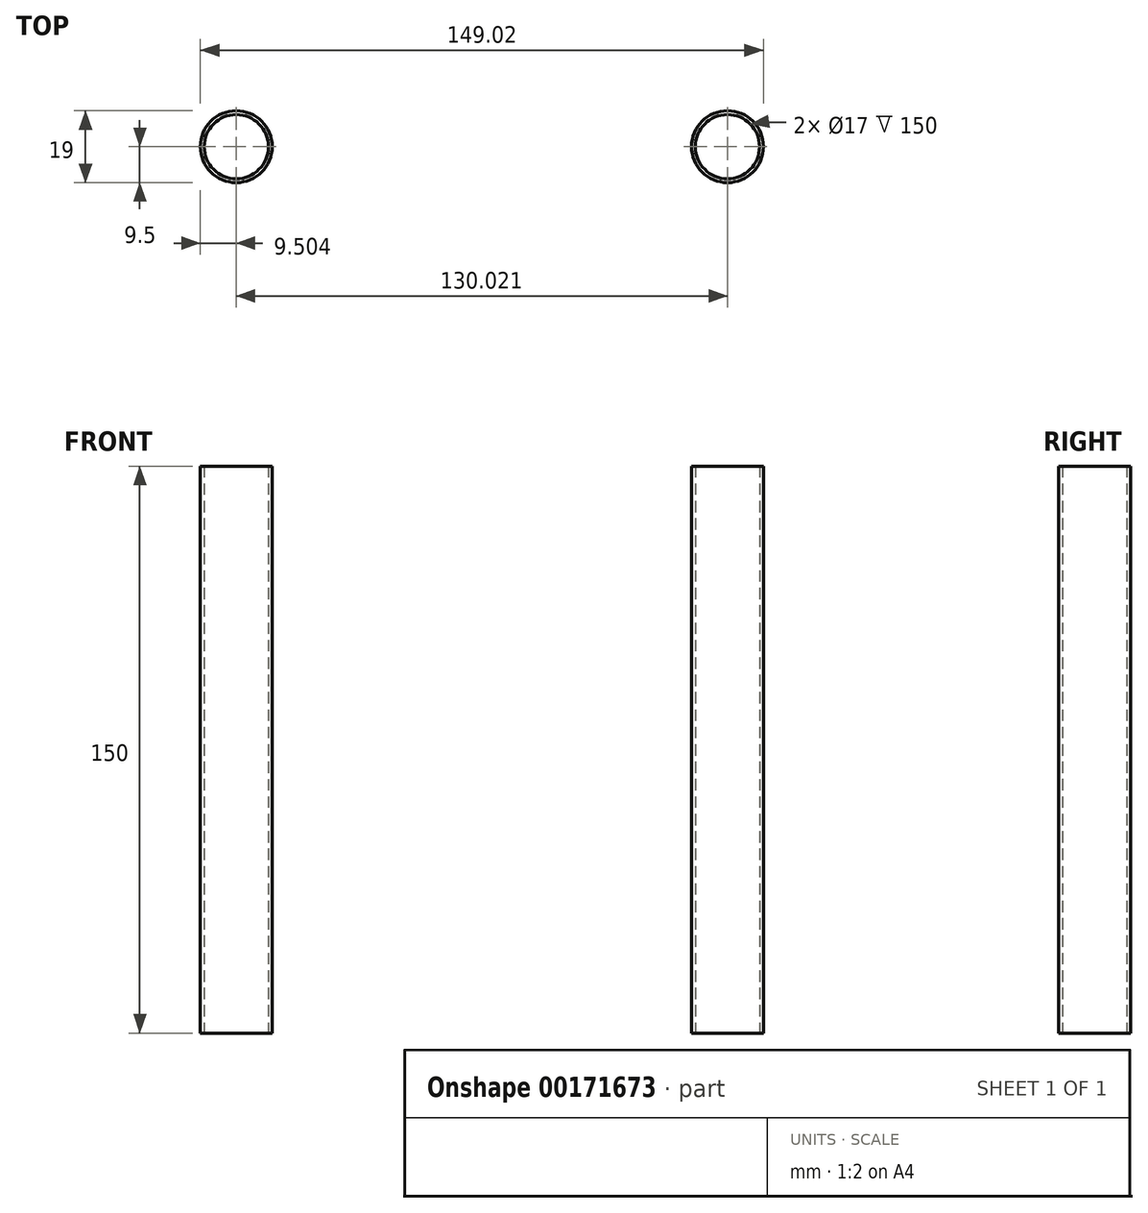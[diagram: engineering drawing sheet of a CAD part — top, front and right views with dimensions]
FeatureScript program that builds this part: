
annotation { "Feature Type Name" : "Feature", "Feature Type Description" : "" }
export const myFeature = defineFeature(function(context is Context, id is Id, definition is map)
    precondition{}
    {
        {
            var Q0;
            Q0=qCreatedBy(makeId("Top.planeOp"),FACE);
            var sketch = newSketch(context, id + "F0", { "sketchPlane" : qUnion([Q0])});
            skCircle(sketch, "E0", {"center": v(0, 0) * mm, "radius": 75 * mm});
            skCircle(sketch, "E1", {"center": v(0, 0) * mm, "radius": 55 * mm});
            skCircle(sketch, "E2", {"center": v(-64.99, 0) * mm, "radius": 9.5 * mm});
            skCircle(sketch, "E3", {"center": v(65.03, 0) * mm, "radius": 9.5 * mm});
            skSolve(sketch);
        }
        {
            var Q0;
            Q0=makeQuery(id+"F0.imprint","IMPRINT",FACE,{"disambiguationData":[TD([[makeQuery(id+"F0.imprint","IMPRINT",EDGE,{"derivedFrom":sQuery(id+"F0.wireOp",EDGE,"E0")}),1.0]])]});
            extrude(context, id + "F1", {"entities" : qUnion([Q0]), "depth" : 150 * mm});
        }
        {
            var Q0;
            Q0=makeQuery(id+"F1.opExtrude","CAP_FACE",FACE,{"disambiguationData":[OSD([sQuery(id+"F0.wireOp",EDGE,"E0"),sQuery(id+"F0.wireOp",EDGE,"E1"),sQuery(id+"F0.wireOp",EDGE,"E2"),sQuery(id+"F0.wireOp",EDGE,"E3")])],"isStart":true});
            var sketch = newSketch(context, id + "F2", { "sketchPlane" : qUnion([Q0])});
            skCircle(sketch, "E4.0", {"center": v(0, 0) * mm, "radius": 75 * mm});
            skSolve(sketch);
        }
        {
            var Q0;
            Q0 = qSketchRegion(id + "F2", true);
            extrude(context, id + "F3", {"entities" : qUnion([Q0]), "operationType" : NewBodyOperationType.ADD, "depth" : 5 * mm});
        }
        {
            var Q0;
            Q0=makeQuery(id+"F1.opExtrude","CAP_FACE",FACE,{"disambiguationData":[OSD([sQuery(id+"F0.wireOp",EDGE,"E0"),sQuery(id+"F0.wireOp",EDGE,"E1"),sQuery(id+"F0.wireOp",EDGE,"E2"),sQuery(id+"F0.wireOp",EDGE,"E3")])],"isStart":false});
            var sketch = newSketch(context, id + "F4", { "sketchPlane" : qUnion([Q0])});
            skCircle(sketch, "E5", {"center": v(65.03, 0) * mm, "radius": 9.5 * mm});
            skCircle(sketch, "E6", {"center": v(65.03, 0) * mm, "radius": 8.5 * mm});
            skCircle(sketch, "E7", {"center": v(-64.99, 0) * mm, "radius": 9.5 * mm});
            skCircle(sketch, "E8", {"center": v(-64.99, 0) * mm, "radius": 8.5 * mm});
            skCircle(sketch, "E9", {"center": v(-6.3, 0) * mm, "radius": 4.6 * mm});
            skSolve(sketch);
        }
        {
            var Q0;
            Q0=sQuery(id+"F4.wireOp",EDGE,"E6");
            extrude(context, id + "F5", {"bodyType" : ToolBodyType.SURFACE, "surfaceEntities" : qUnion([Q0]), "depth" : 150 * mm});
        }
        {
            var Q0;
            Q0 = qSketchRegion(id + "F4", true);
            extrude(context, id + "F6", {"entities" : qUnion([Q0]), "depth" : 150 * mm});
        }
        {
            var Q0;
            Q0=makeQuery(id+"F6.opExtrude","SWEPT_BODY",BODY,{"disambiguationData":[OSD([sQuery(id+"F4.wireOp",EDGE,"E9")])]});
            var Q1;
            Q1=makeQuery(id+"F1.opExtrude","SWEPT_BODY",BODY,{"disambiguationData":[OSD([sQuery(id+"F0.wireOp",EDGE,"E0"),sQuery(id+"F0.wireOp",EDGE,"E1"),sQuery(id+"F0.wireOp",EDGE,"E2"),sQuery(id+"F0.wireOp",EDGE,"E3")])]});
            deleteBodies(context, id + "F7", {"entities" : qUnion([Q0, Q1])});
        }
    });
